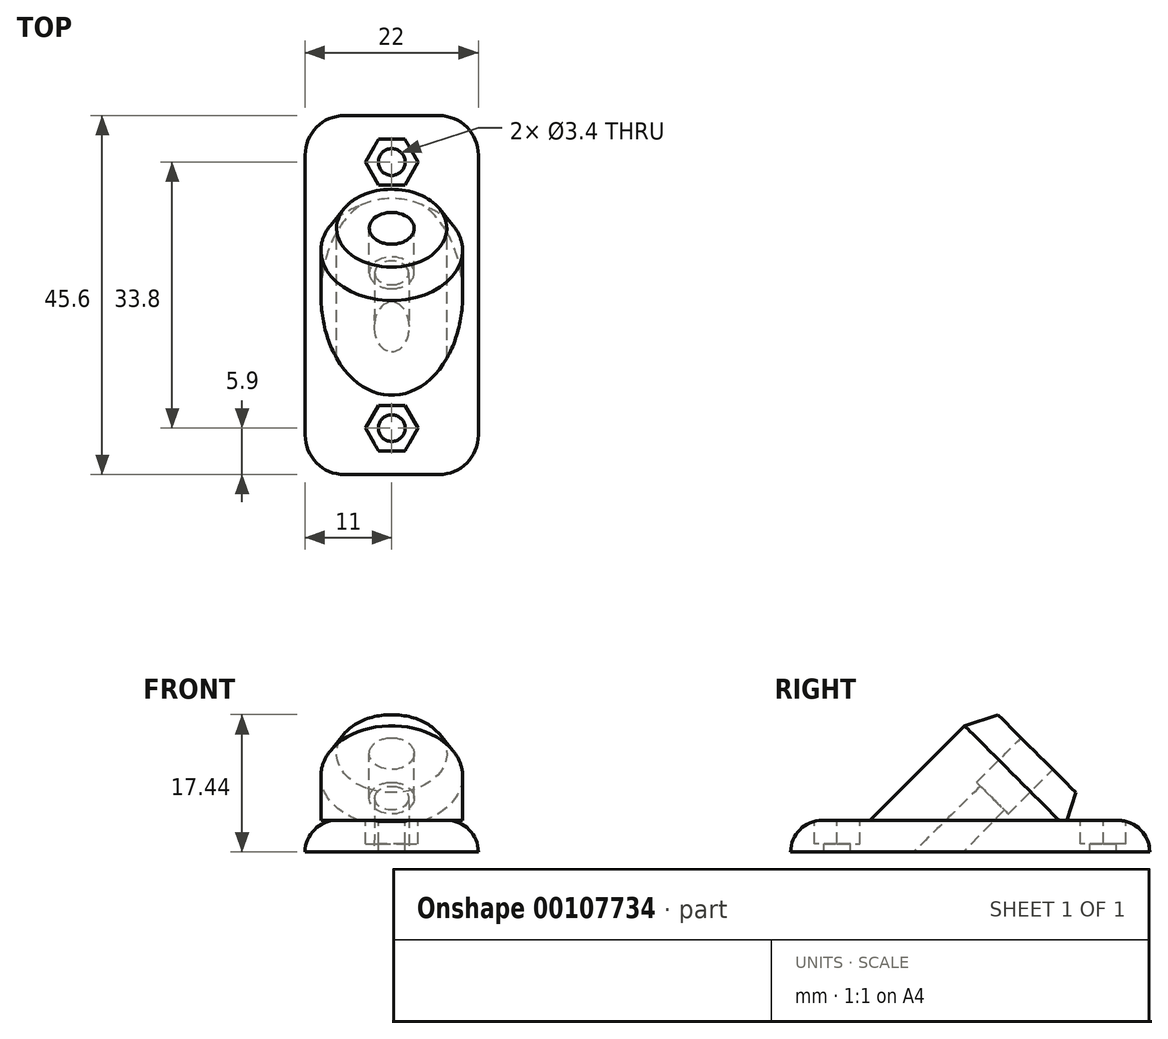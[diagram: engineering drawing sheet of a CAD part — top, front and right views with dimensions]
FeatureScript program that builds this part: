
annotation { "Feature Type Name" : "Feature", "Feature Type Description" : "" }
export const myFeature = defineFeature(function(context is Context, id is Id, definition is map)
    precondition{}
    {
        {
            assignVariable(context, id + "F0", {"name" : "FeederAngle", "anyValue" : 45});
        }
        {
            assignVariable(context, id + "F1", {"name" : "FeederLength", "anyValue" : 12});
        }
        {
            assignVariable(context, id + "F2", {"name" : "PneumatikThreadDepth", "anyValue" : 8});
        }
        {
            var Q0;
            Q0=qCreatedBy(makeId("Top.planeOp"),FACE);
            var sketch = newSketch(context, id + "F3", { "sketchPlane" : qUnion([Q0])});
            skLineSegment(sketch, "E0.bottom", {"start": v(11, -22.8) * mm, "end": v(-11, -22.8) * mm});
            skLineSegment(sketch, "E0.top", {"start": v(11, 22.8) * mm, "end": v(-11, 22.8) * mm});
            skLineSegment(sketch, "E0.left", {"start": v(11, -22.8) * mm, "end": v(11, 22.8) * mm});
            skLineSegment(sketch, "E0.right", {"start": v(-11, -22.8) * mm, "end": v(-11, 22.8) * mm});
            skPoint(sketch, "E0.middle", {"position": v(0, 0) * mm});
            skLineSegment(sketch, "E1", {"start": v(-11, 0) * mm, "end": v(11, 0) * mm, "construction": true});
            skCircle(sketch, "E2", {"center": v(0, 0) * mm, "radius": 9 * mm, "construction": true});
            skCircle(sketch, "E3.cCircle", {"center": v(0, 16.9) * mm, "radius": 2.9 * mm, "construction": true});
            skLineSegment(sketch, "E3.0", {"start": v(3.35, 16.9) * mm, "end": v(1.67, 14) * mm});
            skLineSegment(sketch, "E3.1", {"start": v(1.67, 14) * mm, "end": v(-1.67, 14) * mm});
            skLineSegment(sketch, "E3.2", {"start": v(-1.67, 14) * mm, "end": v(-3.35, 16.9) * mm});
            skLineSegment(sketch, "E3.3", {"start": v(-3.35, 16.9) * mm, "end": v(-1.67, 19.8) * mm});
            skLineSegment(sketch, "E3.4", {"start": v(-1.67, 19.8) * mm, "end": v(1.67, 19.8) * mm});
            skLineSegment(sketch, "E3.5", {"start": v(1.67, 19.8) * mm, "end": v(3.35, 16.9) * mm});
            skPoint(sketch, "E3.0.midPoint", {"position": v(2.51, 15.45) * mm});
            skCircle(sketch, "E4", {"center": v(0, 0) * mm, "radius": 1.7 * mm});
            skLineSegment(sketch, "E5", {"start": v(0, 22.8) * mm, "end": v(0, -22.8) * mm, "construction": true});
            skLineSegment(sketch, "E6.MirrorCS", {"start": v(1.67, -19.8) * mm, "end": v(3.35, -16.9) * mm});
            skCircle(sketch, "E7.MirrorC", {"center": v(0, -16.9) * mm, "radius": 2.9 * mm, "construction": true});
            skLineSegment(sketch, "E8.MirrorCS", {"start": v(-3.35, -16.9) * mm, "end": v(-1.67, -19.8) * mm});
            skLineSegment(sketch, "E9.MirrorCS", {"start": v(-1.67, -19.8) * mm, "end": v(1.67, -19.8) * mm});
            skLineSegment(sketch, "E10.MirrorCS", {"start": v(3.35, -16.9) * mm, "end": v(1.67, -14) * mm});
            skPoint(sketch, "E11.MirrorP", {"position": v(2.51, -15.45) * mm});
            skLineSegment(sketch, "E12.MirrorCS", {"start": v(-1.67, -14) * mm, "end": v(-3.35, -16.9) * mm});
            skLineSegment(sketch, "E13.MirrorCS", {"start": v(1.67, -14) * mm, "end": v(-1.67, -14) * mm});
            skCircle(sketch, "E14", {"center": v(0, 16.9) * mm, "radius": 1.7 * mm});
            skCircle(sketch, "E15.MirrorC", {"center": v(0, -16.9) * mm, "radius": 1.7 * mm});
            skSolve(sketch);
        }
        {
            var Q0;
            Q0=makeQuery(id+"F3.imprint","IMPRINT",FACE,{"disambiguationData":[TD([[makeQuery(id+"F3.imprint","IMPRINT",EDGE,{"derivedFrom":sQuery(id+"F3.wireOp",EDGE,"E0.bottom")}),-1.0]])]});
            var Q1;
            Q1=makeQuery(id+"F3.imprint","IMPRINT",FACE,{"disambiguationData":[TD([[makeQuery(id+"F3.imprint","IMPRINT",EDGE,{"derivedFrom":sQuery(id+"F3.wireOp",EDGE,"E3.0")}),-1.0]])]});
            var Q2;
            Q2=makeQuery(id+"F3.imprint","IMPRINT",FACE,{"disambiguationData":[TD([[makeQuery(id+"F3.imprint","IMPRINT",EDGE,{"derivedFrom":sQuery(id+"F3.wireOp",EDGE,"bd52aa9b-7235-4a46-b349-5895f92444ec0.MirrorCS")}),1.0]])]});
            var Q3;
            Q3=makeQuery(id+"F3.imprint","IMPRINT",FACE,{"disambiguationData":[TD([[makeQuery(id+"F3.imprint","IMPRINT",EDGE,{"derivedFrom":sQuery(id+"F3.wireOp",EDGE,"E4")}),1.0]])]});
            var Q4;
            Q4=makeQuery(id+"F3.imprint","IMPRINT",FACE,{"disambiguationData":[TD([[makeQuery(id+"F3.imprint","IMPRINT",EDGE,{"derivedFrom":sQuery(id+"F3.wireOp",EDGE,"E6.MirrorCS")}),1.0]])]});
            extrude(context, id + "F4", {"entities" : qUnion([Q0, Q1, Q2, Q3, Q4]), "oppositeDirection" : true, "depth" : 4 * mm});
        }
        {
            var Q0;
            Q0=makeQuery(id+"F4.opExtrude","SWEPT_EDGE",EDGE,{"disambiguationData":[OSD([sQuery(id+"F3.wireOp",EDGE,"E0.top"),sQuery(id+"F3.wireOp",EDGE,"E0.right")])]});
            var Q1;
            Q1=makeQuery(id+"F4.opExtrude","SWEPT_EDGE",EDGE,{"disambiguationData":[OSD([sQuery(id+"F3.wireOp",EDGE,"E0.top"),sQuery(id+"F3.wireOp",EDGE,"E0.left")])]});
            var Q2;
            Q2=makeQuery(id+"F4.opExtrude","SWEPT_EDGE",EDGE,{"disambiguationData":[OSD([sQuery(id+"F3.wireOp",EDGE,"E0.bottom"),sQuery(id+"F3.wireOp",EDGE,"E0.left")])]});
            var Q3;
            Q3=makeQuery(id+"F4.opExtrude","SWEPT_EDGE",EDGE,{"disambiguationData":[OSD([sQuery(id+"F3.wireOp",EDGE,"E0.bottom"),sQuery(id+"F3.wireOp",EDGE,"E0.right")])]});
            fillet(context, id + "F5", {"entities" : qUnion([Q0, Q1, Q2, Q3]), "radius" : 5 * mm, "tangentPropagation" : true, "allowEdgeOverflow" : false});
        }
        {
            var Q0;
            Q0=makeQuery(id+"F4.opExtrude","CAP_EDGE",EDGE,{"disambiguationData":[OSD([sQuery(id+"F3.wireOp",EDGE,"E0.right")])],"isStart":true});
            var Q1;
            Q1=makeQuery(id+"F4.opExtrude","CAP_EDGE",EDGE,{"disambiguationData":[OSD([sQuery(id+"F3.wireOp",EDGE,"E0.bottom")])],"isStart":true});
            var Q2;
            {var subQ0=sQuery(id+"F3.wireOp",EDGE,"E0.right");var subQ1=sQuery(id+"F3.wireOp",EDGE,"E0.bottom");Q2=makeQuery(id+"F5.opFillet","BLEND_EDGE",EDGE,{"blendedFrom":[makeQuery(id+"F4.opExtrude","SWEPT_EDGE",EDGE,{"disambiguationData":[OSD([subQ1,subQ0])]}),makeQuery(id+"F4.opExtrude","CAP_FACE",FACE,{"disambiguationData":[OSD([subQ1,sQuery(id+"F3.wireOp",EDGE,"E0.top"),sQuery(id+"F3.wireOp",EDGE,"E0.left"),subQ0,sQuery(id+"F3.wireOp",EDGE,"E14"),sQuery(id+"F3.wireOp",EDGE,"E15.MirrorC")])],"isStart":true})],"blendedInto":[makeQuery(id+"F4.opExtrude","CAP_FACE",FACE,{"disambiguationData":[OSD([subQ1,sQuery(id+"F3.wireOp",EDGE,"E0.top"),sQuery(id+"F3.wireOp",EDGE,"E0.left"),subQ0,sQuery(id+"F3.wireOp",EDGE,"E14"),sQuery(id+"F3.wireOp",EDGE,"E15.MirrorC")])],"isStart":true})]});}
            var Q3;
            {var subQ0=sQuery(id+"F3.wireOp",EDGE,"E0.left");var subQ1=sQuery(id+"F3.wireOp",EDGE,"E0.bottom");Q3=makeQuery(id+"F5.opFillet","BLEND_EDGE",EDGE,{"blendedFrom":[makeQuery(id+"F4.opExtrude","SWEPT_EDGE",EDGE,{"disambiguationData":[OSD([subQ1,subQ0])]}),makeQuery(id+"F4.opExtrude","CAP_FACE",FACE,{"disambiguationData":[OSD([subQ1,sQuery(id+"F3.wireOp",EDGE,"E0.top"),subQ0,sQuery(id+"F3.wireOp",EDGE,"E0.right"),sQuery(id+"F3.wireOp",EDGE,"E14"),sQuery(id+"F3.wireOp",EDGE,"E15.MirrorC")])],"isStart":true})],"blendedInto":[makeQuery(id+"F4.opExtrude","CAP_FACE",FACE,{"disambiguationData":[OSD([subQ1,sQuery(id+"F3.wireOp",EDGE,"E0.top"),subQ0,sQuery(id+"F3.wireOp",EDGE,"E0.right"),sQuery(id+"F3.wireOp",EDGE,"E14"),sQuery(id+"F3.wireOp",EDGE,"E15.MirrorC")])],"isStart":true})]});}
            var Q4;
            Q4=makeQuery(id+"F4.opExtrude","CAP_EDGE",EDGE,{"disambiguationData":[OSD([sQuery(id+"F3.wireOp",EDGE,"E0.left")])],"isStart":true});
            var Q5;
            {var subQ0=sQuery(id+"F3.wireOp",EDGE,"E0.left");var subQ1=sQuery(id+"F3.wireOp",EDGE,"E0.top");Q5=makeQuery(id+"F5.opFillet","BLEND_EDGE",EDGE,{"blendedFrom":[makeQuery(id+"F4.opExtrude","SWEPT_EDGE",EDGE,{"disambiguationData":[OSD([subQ1,subQ0])]}),makeQuery(id+"F4.opExtrude","CAP_FACE",FACE,{"disambiguationData":[OSD([sQuery(id+"F3.wireOp",EDGE,"E0.bottom"),subQ1,subQ0,sQuery(id+"F3.wireOp",EDGE,"E0.right"),sQuery(id+"F3.wireOp",EDGE,"E14"),sQuery(id+"F3.wireOp",EDGE,"E15.MirrorC")])],"isStart":true})],"blendedInto":[makeQuery(id+"F4.opExtrude","CAP_FACE",FACE,{"disambiguationData":[OSD([sQuery(id+"F3.wireOp",EDGE,"E0.bottom"),subQ1,subQ0,sQuery(id+"F3.wireOp",EDGE,"E0.right"),sQuery(id+"F3.wireOp",EDGE,"E14"),sQuery(id+"F3.wireOp",EDGE,"E15.MirrorC")])],"isStart":true})]});}
            var Q6;
            Q6=makeQuery(id+"F4.opExtrude","CAP_EDGE",EDGE,{"disambiguationData":[OSD([sQuery(id+"F3.wireOp",EDGE,"E0.top")])],"isStart":true});
            var Q7;
            {var subQ0=sQuery(id+"F3.wireOp",EDGE,"E0.right");var subQ1=sQuery(id+"F3.wireOp",EDGE,"E0.top");Q7=makeQuery(id+"F5.opFillet","BLEND_EDGE",EDGE,{"blendedFrom":[makeQuery(id+"F4.opExtrude","SWEPT_EDGE",EDGE,{"disambiguationData":[OSD([subQ1,subQ0])]}),makeQuery(id+"F4.opExtrude","CAP_FACE",FACE,{"disambiguationData":[OSD([sQuery(id+"F3.wireOp",EDGE,"E0.bottom"),subQ1,sQuery(id+"F3.wireOp",EDGE,"E0.left"),subQ0,sQuery(id+"F3.wireOp",EDGE,"E14"),sQuery(id+"F3.wireOp",EDGE,"E15.MirrorC")])],"isStart":true})],"blendedInto":[makeQuery(id+"F4.opExtrude","CAP_FACE",FACE,{"disambiguationData":[OSD([sQuery(id+"F3.wireOp",EDGE,"E0.bottom"),subQ1,sQuery(id+"F3.wireOp",EDGE,"E0.left"),subQ0,sQuery(id+"F3.wireOp",EDGE,"E14"),sQuery(id+"F3.wireOp",EDGE,"E15.MirrorC")])],"isStart":true})]});}
            fillet(context, id + "F6", {"entities" : qUnion([Q0, Q1, Q2, Q3, Q4, Q5, Q6, Q7]), "radius" : 4 * mm, "tangentPropagation" : true, "allowEdgeOverflow" : false});
        }
        {
            var Q0;
            Q0=makeQuery(id+"F3.imprint","IMPRINT",FACE,{"disambiguationData":[TD([[makeQuery(id+"F3.imprint","IMPRINT",EDGE,{"derivedFrom":sQuery(id+"F3.wireOp",EDGE,"E3.0")}),-1.0]])]});
            var Q1;
            Q1=makeQuery(id+"F3.imprint","IMPRINT",FACE,{"disambiguationData":[TD([[makeQuery(id+"F3.imprint","IMPRINT",EDGE,{"derivedFrom":sQuery(id+"F3.wireOp",EDGE,"E6.MirrorCS")}),1.0]])]});
            extrude(context, id + "F7", {"entities" : qUnion([Q0, Q1]), "operationType" : NewBodyOperationType.REMOVE, "oppositeDirection" : true, "depth" : 3 * mm});
        }
        {
            var Q0;
            Q0=sQuery(id+"F3.wireOp",EDGE,"E1");
            cPlane(context, id + "F8", {"entities" : qUnion([Q0]), "cplaneType" : CPlaneType.LINE_ANGLE, "offset" : 150 * mm, "angle" : (getVariable(context, 'FeederAngle')) * degree, "width" : 150 * mm, "height" : 150 * mm});
        }
        {
            var Q0;
            Q0=qCreatedBy(id+"F8.planeOp",FACE);
            var sketch = newSketch(context, id + "F9", { "sketchPlane" : qUnion([Q0])});
            skCircle(sketch, "E16", {"center": v(0, 0) * mm, "radius": 9 * mm});
            skSolve(sketch);
        }
        {
            var Q0;
            Q0=qSketchRegion(id+"F9",true);
            var Q1;
            Q1=makeQuery(id+"F4.opExtrude","CAP_FACE",FACE,{"disambiguationData":[OSD([sQuery(id+"F3.wireOp",EDGE,"E0.bottom"),sQuery(id+"F3.wireOp",EDGE,"E0.top"),sQuery(id+"F3.wireOp",EDGE,"E0.left"),sQuery(id+"F3.wireOp",EDGE,"E0.right"),sQuery(id+"F3.wireOp",EDGE,"E4"),sQuery(id+"F3.wireOp",EDGE,"bd52aa9b-7235-4a46-b349-5895f92444ec8.MirrorC")])],"isStart":true});
            extrude(context, id + "F10", {"entities" : qUnion([Q0]), "operationType" : NewBodyOperationType.ADD, "endBound" : BoundingType.UP_TO_SURFACE, "oppositeDirection" : true, "endBoundEntityFace" : qUnion([Q1]), "depth" : 25 * mm, "hasSecondDirection" : true, "secondDirectionOppositeDirection" : false, "secondDirectionDepth" : (getVariable(context, 'FeederLength')) * mm});
        }
        {
            var Q0;
            Q0=makeQuery(id+"F10.opExtrude","CAP_FACE",FACE,{"disambiguationData":[OSD([sQuery(id+"F9.wireOp",EDGE,"E16")])],"isStart":true});
            var sketch = newSketch(context, id + "F11", { "sketchPlane" : qUnion([Q0])});
            skCircle(sketch, "E17", {"center": v(0, 0) * mm, "radius": 2.85 * mm});
            skSolve(sketch);
        }
        {
            var Q0;
            Q0=qSketchRegion(id+"F11",true);
            extrude(context, id + "F12", {"entities" : qUnion([Q0]), "operationType" : NewBodyOperationType.REMOVE, "oppositeDirection" : true, "depth" : (getVariable(context, 'PneumatikThreadDepth')) * mm});
        }
        {
            var Q0;
            Q0=makeQuery(id+"F12.boolean.opBoolean","COPY",FACE,{"derivedFrom":makeQuery(id+"F12.opExtrude","CAP_FACE",FACE,{"disambiguationData":[OSD([sQuery(id+"F11.wireOp",EDGE,"E17")])],"isStart":false})});
            var sketch = newSketch(context, id + "F13", { "sketchPlane" : qUnion([Q0])});
            skCircle(sketch, "E18", {"center": v(0, 0) * mm, "radius": 2.15 * mm});
            skSolve(sketch);
        }
        {
            var Q0;
            Q0=qSketchRegion(id+"F13",true);
            var Q1;
            Q1=makeQuery(id+"F4.opExtrude","CAP_FACE",FACE,{"disambiguationData":[OSD([sQuery(id+"F3.wireOp",EDGE,"E0.bottom"),sQuery(id+"F3.wireOp",EDGE,"E0.top"),sQuery(id+"F3.wireOp",EDGE,"E0.left"),sQuery(id+"F3.wireOp",EDGE,"E0.right"),sQuery(id+"F3.wireOp",EDGE,"E4"),sQuery(id+"F3.wireOp",EDGE,"bd52aa9b-7235-4a46-b349-5895f92444ec8.MirrorC")])],"isStart":false});
            extrude(context, id + "F14", {"entities" : qUnion([Q0]), "operationType" : NewBodyOperationType.REMOVE, "endBound" : BoundingType.UP_TO_SURFACE, "oppositeDirection" : true, "endBoundEntityFace" : qUnion([Q1]), "depth" : 25 * mm, "hasDraft" : true, "draftAngle" : 0.5 * degree});
        }
        {
            var Q0;
            Q0=makeQuery(id+"F10.opExtrude","CAP_EDGE",EDGE,{"disambiguationData":[OSD([sQuery(id+"F9.wireOp",EDGE,"E16")])],"isStart":true});
            chamfer(context, id + "F15", {"entities" : qUnion([Q0]), "chamferType" : ChamferType.TWO_OFFSETS, "width1" : 2 * mm, "oppositeDirection" : false, "width2" : 4 * mm, "tangentPropagation" : true});
        }
    });
